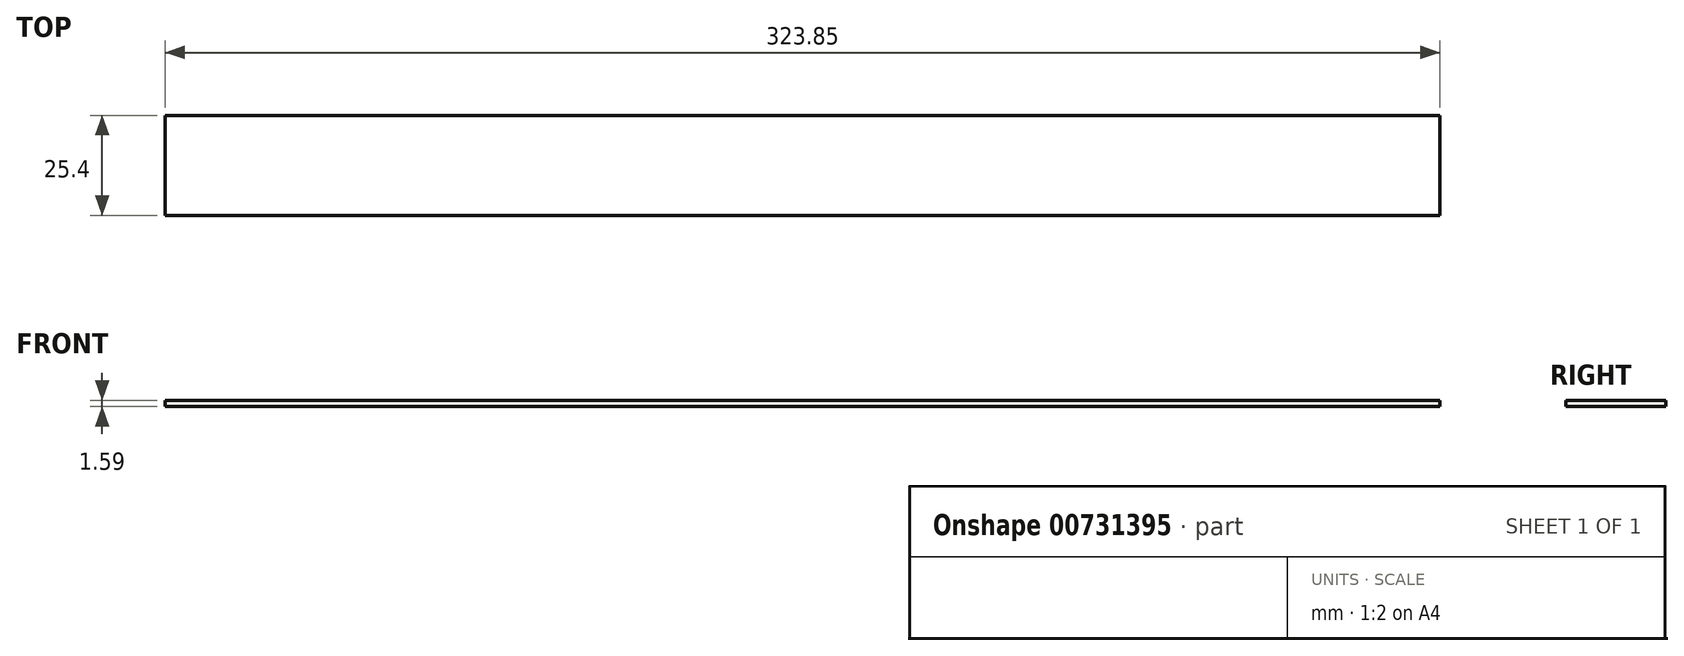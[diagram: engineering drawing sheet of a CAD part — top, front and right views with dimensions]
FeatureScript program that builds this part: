
annotation { "Feature Type Name" : "Feature", "Feature Type Description" : "" }
export const myFeature = defineFeature(function(context is Context, id is Id, definition is map)
    precondition{}
    {
        {
            var Q0;
            Q0=qCreatedBy(makeId("Top.planeOp"),FACE);
            var sketch = newSketch(context, id + "F0", { "sketchPlane" : qUnion([Q0])});
            skLineSegment(sketch, "E0.bottom", {"start": v(0, 0) * mm, "end": v(323.85, 0) * mm});
            skLineSegment(sketch, "E0.top", {"start": v(0, 25.4) * mm, "end": v(323.85, 25.4) * mm});
            skLineSegment(sketch, "E0.left", {"start": v(0, 0) * mm, "end": v(0, 25.4) * mm});
            skLineSegment(sketch, "E0.right", {"start": v(323.85, 0) * mm, "end": v(323.85, 25.4) * mm});
            skLineSegment(sketch, "E1.left", {"start": v(323.85, 25.4) * mm, "end": v(323.85, 0) * mm});
            skSolve(sketch);
        }
        {
            var Q0;
            Q0=makeQuery(id+"F0.imprint","IMPRINT",FACE,{"disambiguationData":[TD([[makeQuery(id+"F0.imprint","IMPRINT",EDGE,{"derivedFrom":sQuery(id+"F0.wireOp",EDGE,"E0.bottom")}),1.0]])]});
            extrude(context, id + "F1", {"entities" : qUnion([Q0]), "depth" : 1.59 * mm, "offsetDistance" : 25.4 * mm});
        }
    });
